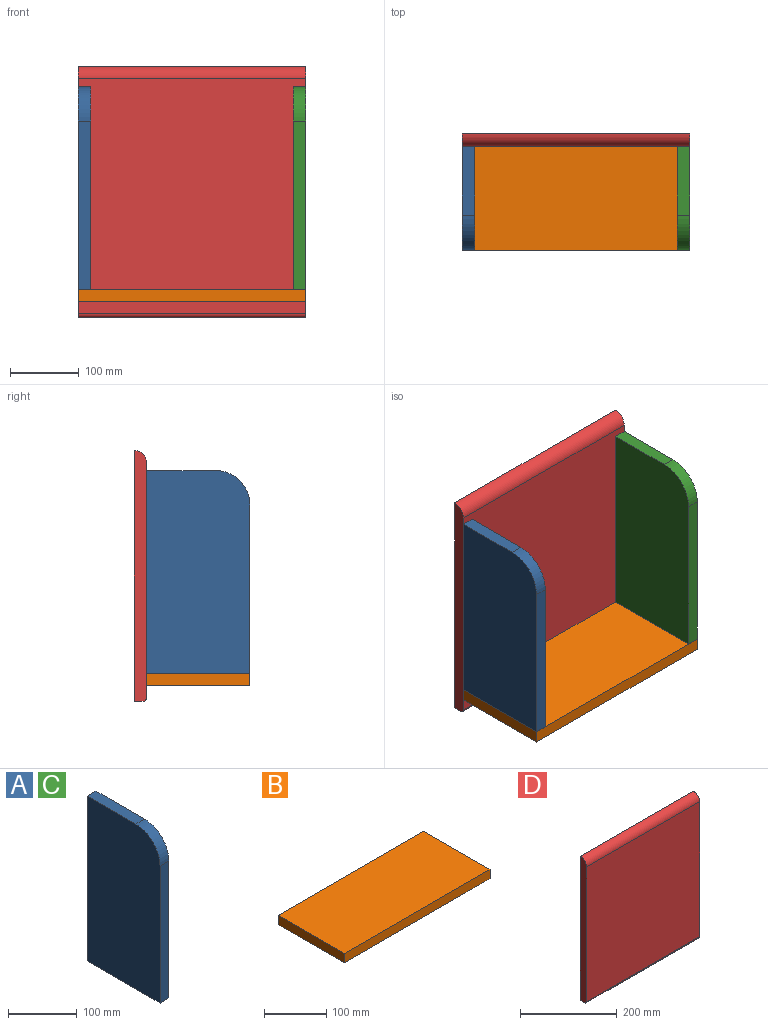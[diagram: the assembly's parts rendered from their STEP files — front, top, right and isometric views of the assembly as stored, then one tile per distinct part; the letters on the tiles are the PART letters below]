
ASSEMBLY  parts=4 mates=3
PART A: 7 faces, bbox 18x150x294 mm
  f0: plane 100x18mm, normal (0,0,1), area 1800mm2, adj f1,f4,f5,f6
  f1: cylinder r=50mm len=50mm, axis (-1,0,0), area 1413.7mm2, adj f0,f2,f5,f6
  f2: plane 244x18mm, normal (0,-1,0), area 4392mm2, adj f1,f3,f5,f6
  f3: plane 150x18mm, normal (0,0,-1), area 2700mm2, adj f2,f4,f5,f6
  f4: plane 294x18mm, normal (0,1,0), area 5292mm2, adj f0,f3,f5,f6
  f5: plane 294x150mm, normal (1,0,0), area 43563.5mm2, adj f0,f1,f2,f3,f4
  f6: plane 294x150mm, normal (-1,0,0), area 43563.5mm2, adj f0,f1,f2,f3,f4
PART B: 6 faces, bbox 330x150x18 mm
  f0: plane 330x18mm, normal (0,1,0), area 5940mm2, adj f1,f3,f4,f5
  f1: plane 150x18mm, normal (-1,0,0), area 2700mm2, adj f0,f2,f4,f5
  f2: plane 330x18mm, normal (0,-1,0), area 5940mm2, adj f1,f3,f4,f5
  f3: plane 150x18mm, normal (1,0,0), area 2700mm2, adj f0,f2,f4,f5
  f4: plane 330x150mm, normal (0,0,1), area 49500mm2, adj f0,f1,f2,f3
  f5: plane 330x150mm, normal (0,0,-1), area 49500mm2, adj f0,f1,f2,f3
PART C: same geometry as A
PART D: 7 faces, bbox 330x18x364 mm
  f0: plane 364x18mm, normal (-1,0,0), area 6477.1mm2, adj f1,f3,f4,f5,f6
  f1: plane 330x13mm, normal (0,0,-1), area 4290mm2, adj f0,f2,f4,f5
  f2: plane 364x18mm, normal (1,0,0), area 6477.1mm2, adj f1,f3,f4,f5,f6
  f3: plane 341x330mm, normal (0,-1,0), area 112530mm2, adj f0,f2,f5,f6
  f4: plane 364x330mm, normal (0,1,0), area 120120mm2, adj f0,f1,f2,f6
  f5: cylinder r=5mm len=330mm, axis (-1,0,0), area 2591.8mm2, adj f0,f1,f2,f3
  f6: cylinder r=18mm len=330mm, axis (1,0,0), area 9330.5mm2, adj f0,f2,f3,f4
PLACE A t=(-196.63,-225.18,-1.46)mm
PLACE B t=(-6.64,-56.04,-98.74)mm
PLACE C t=(115.37,-225.18,-1.46)mm
PLACE D t=(-22.51,49.14,1.88)mm
MATE fastened B.f0 <-> D.f3  axis (0,1,0) through (-31.63,31.14,-98.74)mm
MATE fastened A.f3 <-> B.f4  axis (0,0,-1) through (-196.63,-43.86,-80.74)mm
MATE fastened C.f3 <-> B.f4  axis (0,0,-1) through (133.37,-43.86,-80.74)mm
